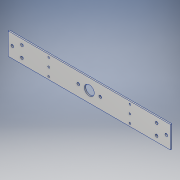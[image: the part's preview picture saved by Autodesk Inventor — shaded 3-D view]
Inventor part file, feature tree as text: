
AUTODESK INVENTOR PART (.ipt)
format: ipt  version: 2017 (Build 210142000, 142)  size: 146,944 bytes
history: native  units: in
note: dims shown in document units (in); Inventor stores cm internally (conversion verified against a paired STEP export)
features: hole x3, sketch x3, extrude x1
ambient origin geometry x8: Origin, YZ Plane, XZ Plane, XY Plane, X Axis, Y Axis, Z Axis, Center Point
bodies: Body1 (feature_tree)
feature tree (7):
  extrude  "Extrusion2"  Depth=14.75in
  hole  "Hole1"  [1 undecoded]
  hole  "Hole2"  [1 undecoded]
  hole  "Hole3"  [1 undecoded]
  sketch  "Sketch3"  dims[d0=14.75in d3=0.5in]
  sketch  "Sketch4"  dims[d4=1.0in d5=0.25in]
  sketch  "Sketch5"  dims[d6=0.25in d10=0.25in d11=1.25in d12=0.125in d13=0.0in d14=0.9in d15=0.75in d16=0.375in d17=0.25in d18=0.5635in d19=1.0in d20=0.8108in d21=1.0in d22=0.25in d23=0.25in d24=0.75in d25=0.375in d26=0.25in d27=0.5635in d28=1.0in d29=0.8108in d30=3.689in d31=0.25in d32=0.75in d33=0.163in d34=0.75in d35=0.163in d36=0.163in d37=0.163in d38=0.75in d39=0.375in d40=0.25in d41=0.5635in d42=1.0in d43=0.8108in]
note: 3 required parameter values undecoded (feature->parameter linkage not recoverable at this tier; creation-order binding heuristic only, values carry confidence <= 0.55)
